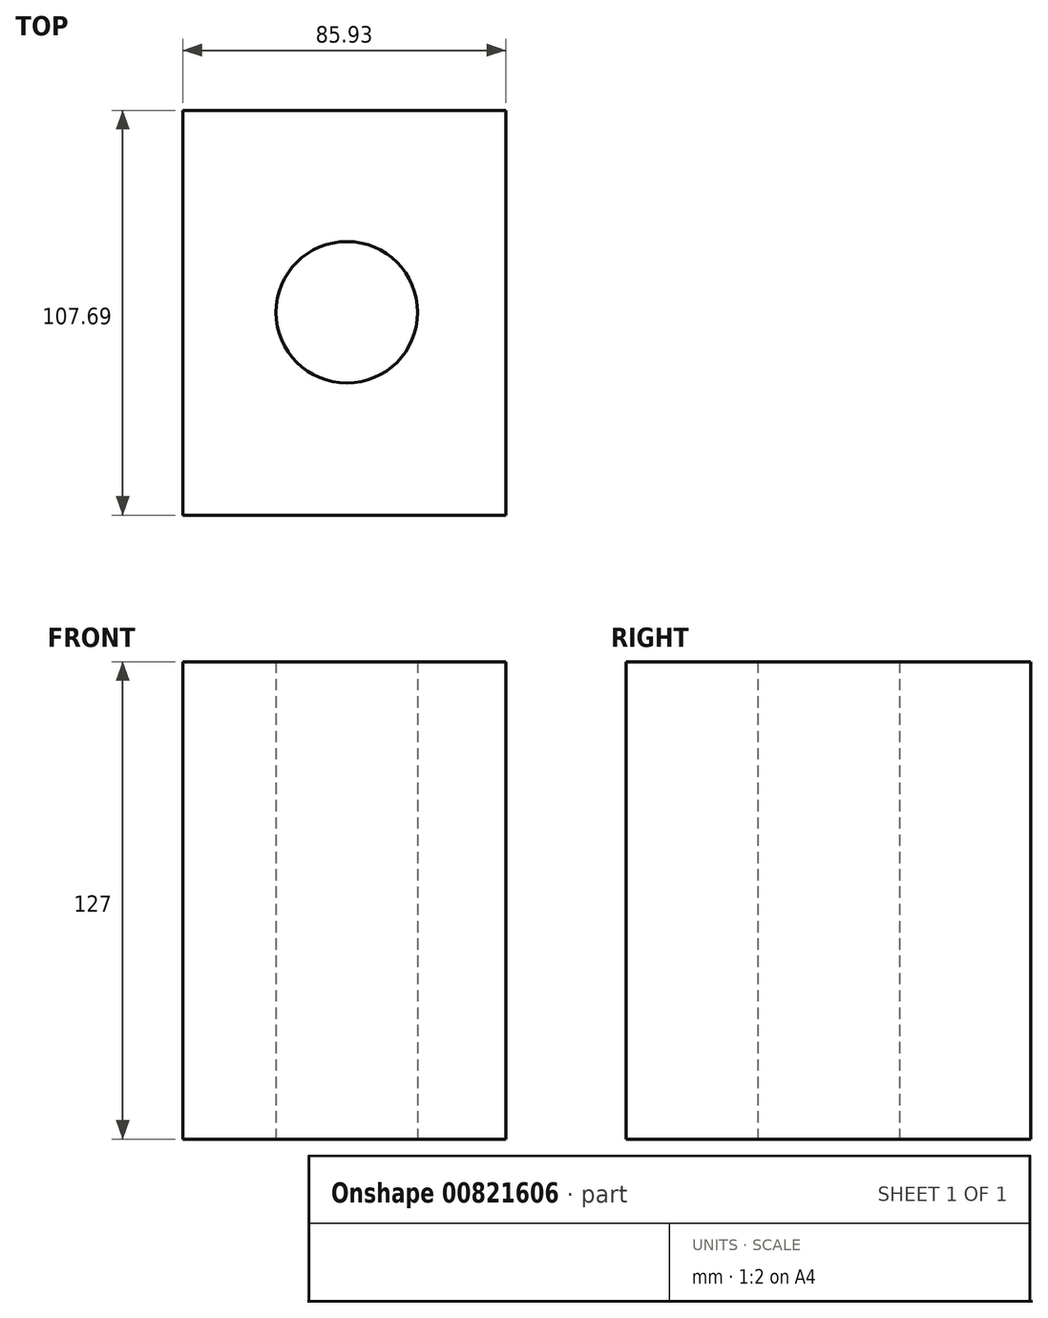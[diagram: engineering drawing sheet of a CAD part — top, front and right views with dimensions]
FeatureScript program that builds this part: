
annotation { "Feature Type Name" : "Feature", "Feature Type Description" : "" }
export const myFeature = defineFeature(function(context is Context, id is Id, definition is map)
    precondition{}
    {
        {
            var Q0;
            Q0=qCreatedBy(makeId("Top.planeOp"),FACE);
            var sketch = newSketch(context, id + "F0", { "sketchPlane" : qUnion([Q0])});
            skLineSegment(sketch, "E0.bottom", {"start": v(-43.63, 53.75) * mm, "end": v(42.3, 53.75) * mm});
            skLineSegment(sketch, "E0.top", {"start": v(-43.63, -53.94) * mm, "end": v(42.3, -53.94) * mm});
            skLineSegment(sketch, "E0.left", {"start": v(-43.63, 53.75) * mm, "end": v(-43.63, -53.94) * mm});
            skLineSegment(sketch, "E0.right", {"start": v(42.3, 53.75) * mm, "end": v(42.3, -53.94) * mm});
            skCircle(sketch, "E1", {"center": v(0, 0) * mm, "radius": 18.83 * mm});
            skSolve(sketch);
        }
        {
            var Q0;
            Q0=makeQuery(id+"F0.imprint","IMPRINT",FACE,{"disambiguationData":[TD([[makeQuery(id+"F0.imprint","IMPRINT",EDGE,{"derivedFrom":sQuery(id+"F0.wireOp",EDGE,"E0.bottom")}),-1.0]])]});
            extrude(context, id + "F1", {"entities" : qUnion([Q0]), "depth" : 127 * mm, "offsetDistance" : 25.4 * mm});
        }
    });
